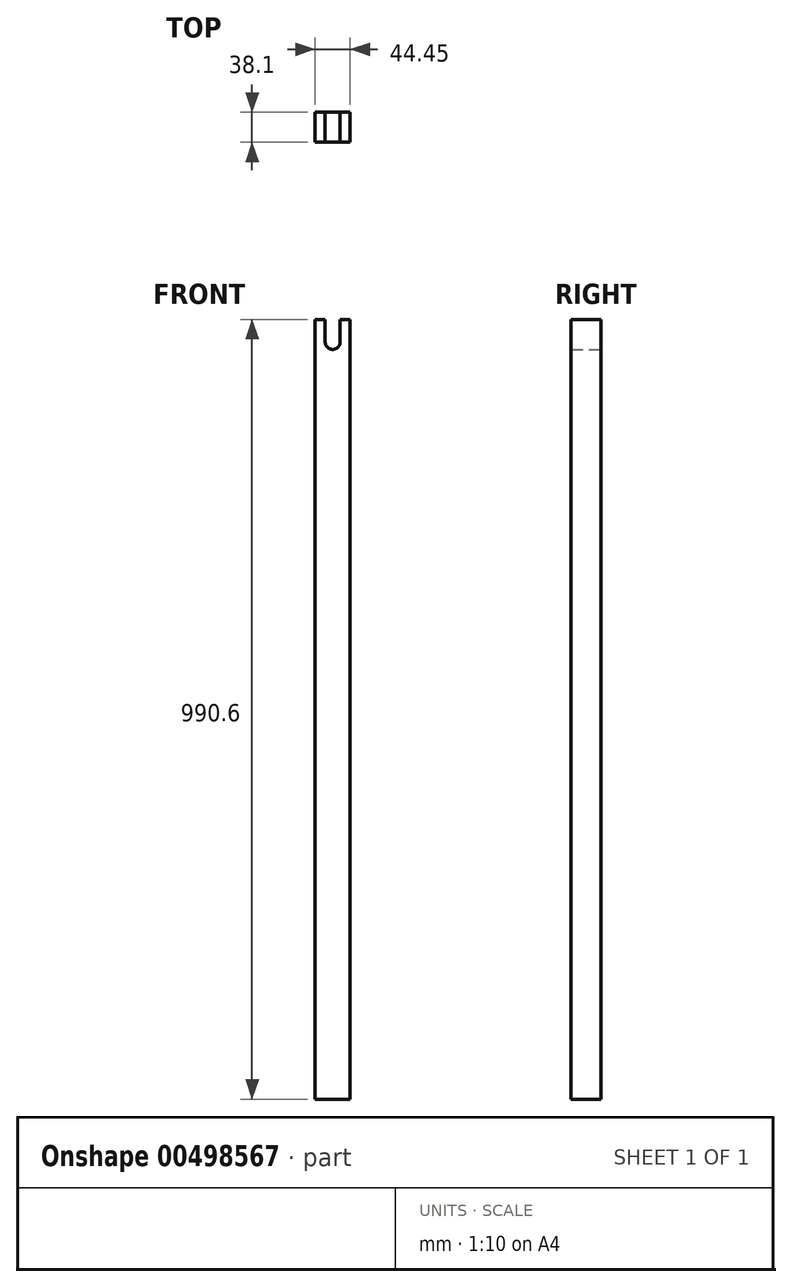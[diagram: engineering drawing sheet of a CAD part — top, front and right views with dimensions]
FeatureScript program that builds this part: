
annotation { "Feature Type Name" : "Feature", "Feature Type Description" : "" }
export const myFeature = defineFeature(function(context is Context, id is Id, definition is map)
    precondition{}
    {
        {
            var Q0;
            Q0=qCreatedBy(makeId("Front.planeOp"),FACE);
            var sketch = newSketch(context, id + "F0", { "sketchPlane" : qUnion([Q0])});
            skLineSegment(sketch, "E0.bottom", {"start": v(0, 0) * mm, "end": v(44.45, 0) * mm});
            skLineSegment(sketch, "E0.top", {"start": v(0, 990.6) * mm, "end": v(44.45, 990.6) * mm});
            skLineSegment(sketch, "E0.left", {"start": v(0, 0) * mm, "end": v(0, 990.6) * mm});
            skLineSegment(sketch, "E0.right", {"start": v(44.45, 0) * mm, "end": v(44.45, 990.6) * mm});
            skSolve(sketch);
        }
        {
            var Q0;
            Q0 = qSketchRegion(id + "F0", true);
            extrude(context, id + "F1", {"entities" : qUnion([Q0]), "depth" : 38.1 * mm, "offsetDistance" : 25.4 * mm});
        }
        {
            var Q0;
            Q0=makeQuery(id+"F1.opExtrude","CAP_FACE",FACE,{"disambiguationData":[OSD([sQuery(id+"F0.wireOp",EDGE,"E0.bottom"),sQuery(id+"F0.wireOp",EDGE,"E0.top"),sQuery(id+"F0.wireOp",EDGE,"E0.left"),sQuery(id+"F0.wireOp",EDGE,"E0.right")])],"isStart":false});
            var sketch = newSketch(context, id + "F2", { "sketchPlane" : qUnion([Q0])});
            skLineSegment(sketch, "E1.bottom", {"start": v(12.7, 990.6) * mm, "end": v(31.75, 990.6) * mm});
            skLineSegment(sketch, "E1.top", {"start": v(12.7, 952.5) * mm, "end": v(31.75, 952.5) * mm});
            skLineSegment(sketch, "E1.left", {"start": v(12.7, 990.6) * mm, "end": v(12.7, 952.5) * mm});
            skLineSegment(sketch, "E1.right", {"start": v(31.75, 990.6) * mm, "end": v(31.75, 952.5) * mm});
            skSolve(sketch);
        }
        {
            var Q0;
            Q0 = qSketchRegion(id + "F2", true);
            extrude(context, id + "F3", {"entities" : qUnion([Q0]), "operationType" : NewBodyOperationType.REMOVE, "endBound" : BoundingType.THROUGH_ALL, "oppositeDirection" : true, "depth" : 25.4 * mm, "offsetDistance" : 25.4 * mm});
        }
        {
            var Q0;
            Q0=makeQuery(id+"F3.boolean.opBoolean","COPY",EDGE,{"derivedFrom":makeQuery(id+"F3.opExtrude","SWEPT_EDGE",EDGE,{"disambiguationData":[OSD([sQuery(id+"F2.wireOp",EDGE,"E1.top"),sQuery(id+"F2.wireOp",EDGE,"E1.left")])]})});
            var Q1;
            Q1=makeQuery(id+"F3.boolean.opBoolean","COPY",EDGE,{"derivedFrom":makeQuery(id+"F3.opExtrude","SWEPT_EDGE",EDGE,{"disambiguationData":[OSD([sQuery(id+"F2.wireOp",EDGE,"E1.top"),sQuery(id+"F2.wireOp",EDGE,"E1.right")])]})});
            fillet(context, id + "F4", {"entities" : qUnion([Q0, Q1]), "radius" : 9.52 * mm, "tangentPropagation" : true, "allowEdgeOverflow" : false});
        }
    });
